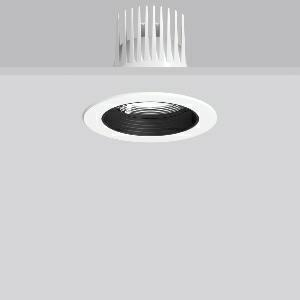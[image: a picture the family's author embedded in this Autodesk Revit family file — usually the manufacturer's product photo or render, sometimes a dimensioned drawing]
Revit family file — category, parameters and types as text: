
# Revit family: heledon_maxi_e_901767_002_1_76_b903
name_source: partatom
category: Lighting Fixtures
units: mm (PartAtom-declared; Revit-internal decimal feet)

## family parameters
Cut with Voids When Loaded = No
Host = Face
Light Source = No
Part Type = Normal
Room Calculation Point = No
Round Connector Dimension = Use Diameter
Shared = No

## types (1)
- HELEDON maxi E (1 x LED Modul 940, 3900 lm, 4000)
    Apparent Load = 35 VA
    Approval mark = CE
    CIE Flux Codes = 97 100 100 100 100
    Color Rendering = 92
    Color Temperature = 4000
    Default Elevation = 1800 mm
    Description = Series: HELEDON maxi
Round recessed downlight. Housing: die-cast aluminium, powder-coated. Black plastic ring and recessed LED to prevent glare from the side. Optical assembly with lens made of plastic (polycarbonate) for the best homogeneous light distribution - can be changed without tools. Best colour rendering index Ra>90. Suitable for Recessed ceiling mounting. Installation without tools thanks to spring fastening system. Including separate LED converter with connecting cable 600 mm.High quality converter without flickering and stroboscopic effect. Through-wiring box (5 pole) available as accessory. The following accessories can be mounted without use of tools: interchangeable lenses, decorative glasses, honeycomb louvre, clear and frosted diffusers, white interchangeable plastic ring. 
Colour: traffic white, matt (RAL 9016)
Diameter: 162 mm
Height: 3 mm
Cut-out diameter: 152 mm
Recess height: 200 mm
Luminaire: recess height: 135 mm
Lamp: LED
Socket: without socket
Colour temperature: 4000K
Colour rendering index (CRI): 92
System power: 35 W
Rated luminous flux: 3900 lm
Luminous efficiency: 111 lm/W
Control gear: Converter, dimmable, DALI
Protection class: II
Type of protection: IP 20
    Height = 0 mm  [stored 0 ft]
    Lamp = 1 x LED Modul 940
    Lamp Light Flux = 3900 lm
    Lamp count = 1
    Length = 162 mm
    Lifetime = 50000 h
    Luminous efficacy = 111 lm/W
    Manufacturer = RZB
    ModVariant = No
    Model = 901767.002.1.76
    Mounting Place = Ceiling
    Mounting Type = Recessed
    Number of Poles = 1
    OnlyDefault = Yes
    Power Factor = 1
    Product Name = HELEDON maxi E
    Product group = Recessed downlights
    ProductGroupID = 402
    Protection Class = Protection class II
    Protection Degree = IP 20
    RLX_Detail_Level = 1
    RLX_Emergency_Light_Flux = 0 lm
    RLX_Emergency_Type = 0
    RLX_Emergency_Type_DB = No
    RlxData = <blob elided: 121077 chars, md5=0aaa3585>
    Socket = socket
    Standby Power = 0 W
    System Light Flux = 3900 lm
    System Power = 35 W
    Type Comments = Product without accessories
    Type Image = 901663.002.jpg
    URL = http://relux.com
    VarID = ---
    Voltage = 230 V
    Voltage Range = 220-240 V
    Weight = 0.00 kg
    Width = 0 mm  [stored 0 ft]

note: [stored X ft] marks values corroborated as IEEE doubles in the binary element streams (Revit-internal decimal feet)

## geometry (parser evidence)
native form markers: Blend x4, Sweep x11
no freeform markers — native parametric forms only
